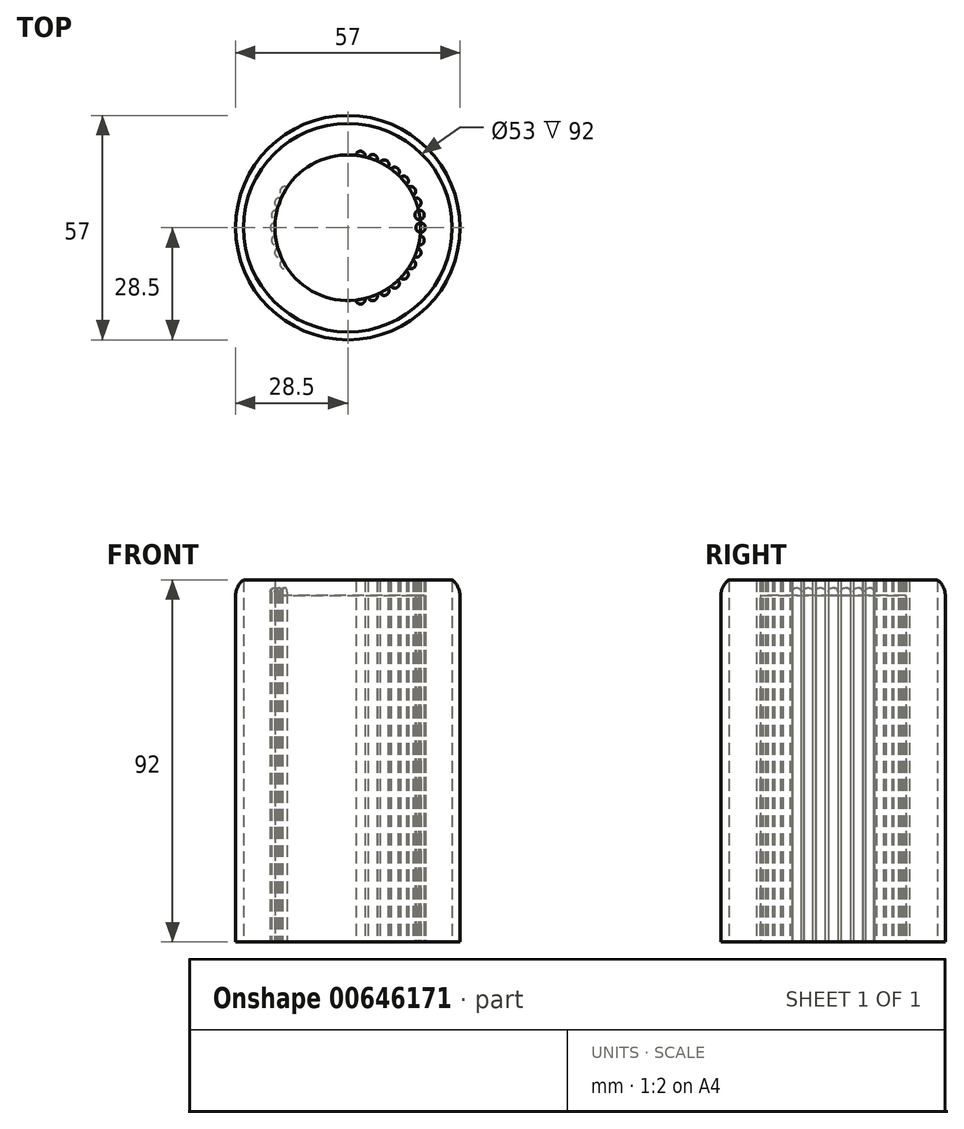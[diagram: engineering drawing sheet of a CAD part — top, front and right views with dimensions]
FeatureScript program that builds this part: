
annotation { "Feature Type Name" : "Feature", "Feature Type Description" : "" }
export const myFeature = defineFeature(function(context is Context, id is Id, definition is map)
    precondition{}
    {
        {
            var Q0;
            Q0=qCreatedBy(makeId("Top.planeOp"),FACE);
            var sketch = newSketch(context, id + "F0", { "sketchPlane" : qUnion([Q0])});
            skCircle(sketch, "E0", {"center": v(0, 0) * mm, "radius": 28.5 * mm});
            skCircle(sketch, "E1", {"center": v(0, 0) * mm, "radius": 26.5 * mm});
            skCircle(sketch, "E2", {"center": v(0, 0) * mm, "radius": 18.5 * mm});
            skLineSegment(sketch, "E3", {"start": v(-44.15, 0) * mm, "end": v(45.98, 0) * mm, "construction": true});
            skPoint(sketch, "E4", {"position": v(-18.5, 0) * mm});
            skCircle(sketch, "E5", {"center": v(-18.5, 0) * mm, "radius": 1.2 * mm});
            skCircle(sketch, "E6.1.0", {"center": v(-18.22, 3.21) * mm, "radius": 1.2 * mm});
            skCircle(sketch, "E6.2.0", {"center": v(-17.38, 6.33) * mm, "radius": 1.2 * mm});
            skLineSegment(sketch, "E6.anchor1", {"start": v(0, 0) * mm, "end": v(-18.5, 0) * mm, "construction": true});
            skLineSegment(sketch, "E6.anchor2", {"start": v(0, 0) * mm, "end": v(-18.22, -3.21) * mm, "construction": true});
            skCircle(sketch, "E7.1.3.0", {"center": v(-16.02, 9.25) * mm, "radius": 1.2 * mm});
            skCircle(sketch, "E7.1.4.0", {"center": v(-14.17, 11.9) * mm, "radius": 1.2 * mm});
            skCircle(sketch, "E7.1.5.0", {"center": v(-11.9, 14.17) * mm, "radius": 1.2 * mm});
            skCircle(sketch, "E7.1.6.0", {"center": v(-9.25, 16.02) * mm, "radius": 1.2 * mm});
            skCircle(sketch, "E7.1.7.0", {"center": v(-6.33, 17.38) * mm, "radius": 1.2 * mm});
            skCircle(sketch, "E7.1.8.0", {"center": v(-3.21, 18.22) * mm, "radius": 1.2 * mm});
            skCircle(sketch, "E7.1.9.0", {"center": v(0, 18.5) * mm, "radius": 1.2 * mm});
            skCircle(sketch, "E7.1.10.0", {"center": v(3.21, 18.22) * mm, "radius": 1.2 * mm});
            skCircle(sketch, "E7.1.11.0", {"center": v(6.33, 17.38) * mm, "radius": 1.2 * mm});
            skCircle(sketch, "E7.1.12.0", {"center": v(9.25, 16.02) * mm, "radius": 1.2 * mm});
            skCircle(sketch, "E7.1.13.0", {"center": v(11.9, 14.17) * mm, "radius": 1.2 * mm});
            skCircle(sketch, "E7.1.14.0", {"center": v(14.17, 11.9) * mm, "radius": 1.2 * mm});
            skCircle(sketch, "E7.1.15.0", {"center": v(16.02, 9.25) * mm, "radius": 1.2 * mm});
            skCircle(sketch, "E7.1.16.0", {"center": v(17.38, 6.33) * mm, "radius": 1.2 * mm});
            skCircle(sketch, "E7.1.17.0", {"center": v(18.22, 3.21) * mm, "radius": 1.2 * mm});
            skCircle(sketch, "E7.1.18.0", {"center": v(18.5, 0) * mm, "radius": 1.2 * mm});
            skCircle(sketch, "E7.1.19.0", {"center": v(18.22, -3.21) * mm, "radius": 1.2 * mm});
            skCircle(sketch, "E7.1.20.0", {"center": v(17.38, -6.33) * mm, "radius": 1.2 * mm});
            skCircle(sketch, "E7.1.21.0", {"center": v(16.02, -9.25) * mm, "radius": 1.2 * mm});
            skCircle(sketch, "E7.1.22.0", {"center": v(14.17, -11.9) * mm, "radius": 1.2 * mm});
            skCircle(sketch, "E7.1.23.0", {"center": v(11.9, -14.17) * mm, "radius": 1.2 * mm});
            skCircle(sketch, "E7.1.24.0", {"center": v(9.25, -16.02) * mm, "radius": 1.2 * mm});
            skCircle(sketch, "E7.1.25.0", {"center": v(6.33, -17.38) * mm, "radius": 1.2 * mm});
            skCircle(sketch, "E7.1.26.0", {"center": v(3.21, -18.22) * mm, "radius": 1.2 * mm});
            skCircle(sketch, "E7.1.27.0", {"center": v(0, -18.5) * mm, "radius": 1.2 * mm});
            skCircle(sketch, "E7.1.28.0", {"center": v(-3.21, -18.22) * mm, "radius": 1.2 * mm});
            skCircle(sketch, "E7.1.29.0", {"center": v(-6.33, -17.38) * mm, "radius": 1.2 * mm});
            skCircle(sketch, "E8.1.30.0", {"center": v(-9.25, -16.02) * mm, "radius": 1.2 * mm});
            skCircle(sketch, "E8.1.31.0", {"center": v(-11.9, -14.17) * mm, "radius": 1.2 * mm});
            skCircle(sketch, "E8.1.32.0", {"center": v(-14.17, -11.9) * mm, "radius": 1.2 * mm});
            skCircle(sketch, "E8.1.33.0", {"center": v(-16.02, -9.25) * mm, "radius": 1.2 * mm});
            skCircle(sketch, "E8.1.34.0", {"center": v(-17.38, -6.33) * mm, "radius": 1.2 * mm});
            skCircle(sketch, "E8.1.35.0", {"center": v(-18.22, -3.21) * mm, "radius": 1.2 * mm});
            skSolve(sketch);
        }
        {
            var Q0;
            Q0=makeQuery(id+"F0.imprint","IMPRINT",FACE,{"disambiguationData":[TD([[makeQuery(id+"F0.imprint","IMPRINT",EDGE,{"derivedFrom":sQuery(id+"F0.wireOp",EDGE,"E0")}),1.0]])]});
            extrude(context, id + "F1", {"entities" : qUnion([Q0]), "depth" : 92 * mm, "offsetDistance" : 25 * mm});
        }
        {
            var Q0;
            Q0=makeQuery(id+"F1.opExtrude","CAP_EDGE",EDGE,{"disambiguationData":[OSD([sQuery(id+"F0.wireOp",EDGE,"E0")])],"isStart":false});
            fillet(context, id + "F2", {"entities" : qUnion([Q0]), "radius" : 5 * mm, "tangentPropagation" : true, "allowEdgeOverflow" : false});
        }
        {
            var Q0;
            Q0=makeQuery(id+"F0.imprint","IMPRINT",FACE,{"disambiguationData":[TD([[makeQuery(id+"F0.imprint","IMPRINT",EDGE,{"derivedFrom":sQuery(id+"F0.wireOp",EDGE,"E1")}),1.0]])]});
            var Q1;
            {var subQ0=sQuery(id+"F0.wireOp",EDGE,"E2");var subQ1=sQuery(id+"F0.wireOp",EDGE,"E6.1.0");var subQ2=makeQuery(id+"F0.imprint","INTERSECT",VERTEX,{"disambiguationData":[OD(0.0)],"derivedFrom":[subQ1,subQ0]});Q1=makeQuery(id+"F0.imprint","IMPRINT",FACE,{"disambiguationData":[TD([[makeQuery(id+"F0.imprint","IMPRINT",EDGE,{"disambiguationData":[TD([[subQ2,-1.0]])],"derivedFrom":subQ1}),1.0]])]});}
            var Q2;
            {var subQ0=sQuery(id+"F0.wireOp",EDGE,"E2");var subQ1=sQuery(id+"F0.wireOp",EDGE,"E6.2.0");var subQ2=makeQuery(id+"F0.imprint","INTERSECT",VERTEX,{"disambiguationData":[OD(0.0)],"derivedFrom":[subQ1,subQ0]});Q2=makeQuery(id+"F0.imprint","IMPRINT",FACE,{"disambiguationData":[TD([[makeQuery(id+"F0.imprint","IMPRINT",EDGE,{"disambiguationData":[TD([[subQ2,-1.0]])],"derivedFrom":subQ1}),1.0]])]});}
            var Q3;
            {var subQ0=sQuery(id+"F0.wireOp",EDGE,"E2");var subQ1=sQuery(id+"F0.wireOp",EDGE,"E7.1.3.0");var subQ2=makeQuery(id+"F0.imprint","INTERSECT",VERTEX,{"disambiguationData":[OD(0.0)],"derivedFrom":[subQ1,subQ0]});Q3=makeQuery(id+"F0.imprint","IMPRINT",FACE,{"disambiguationData":[TD([[makeQuery(id+"F0.imprint","IMPRINT",EDGE,{"disambiguationData":[TD([[subQ2,-1.0]])],"derivedFrom":subQ1}),1.0]])]});}
            var Q4;
            {var subQ0=sQuery(id+"F0.wireOp",EDGE,"E2");var subQ1=sQuery(id+"F0.wireOp",EDGE,"E7.1.4.0");var subQ2=makeQuery(id+"F0.imprint","INTERSECT",VERTEX,{"disambiguationData":[OD(0.0)],"derivedFrom":[subQ1,subQ0]});Q4=makeQuery(id+"F0.imprint","IMPRINT",FACE,{"disambiguationData":[TD([[makeQuery(id+"F0.imprint","IMPRINT",EDGE,{"disambiguationData":[TD([[subQ2,-1.0]])],"derivedFrom":subQ1}),1.0]])]});}
            var Q5;
            {var subQ0=sQuery(id+"F0.wireOp",EDGE,"E2");var subQ1=sQuery(id+"F0.wireOp",EDGE,"E7.1.5.0");var subQ2=makeQuery(id+"F0.imprint","INTERSECT",VERTEX,{"disambiguationData":[OD(0.0)],"derivedFrom":[subQ1,subQ0]});Q5=makeQuery(id+"F0.imprint","IMPRINT",FACE,{"disambiguationData":[TD([[makeQuery(id+"F0.imprint","IMPRINT",EDGE,{"disambiguationData":[TD([[subQ2,-1.0]])],"derivedFrom":subQ1}),1.0]])]});}
            var Q6;
            {var subQ0=sQuery(id+"F0.wireOp",EDGE,"E2");var subQ1=sQuery(id+"F0.wireOp",EDGE,"E7.1.6.0");var subQ2=makeQuery(id+"F0.imprint","INTERSECT",VERTEX,{"disambiguationData":[OD(0.0)],"derivedFrom":[subQ1,subQ0]});Q6=makeQuery(id+"F0.imprint","IMPRINT",FACE,{"disambiguationData":[TD([[makeQuery(id+"F0.imprint","IMPRINT",EDGE,{"disambiguationData":[TD([[subQ2,-1.0]])],"derivedFrom":subQ1}),1.0]])]});}
            var Q7;
            {var subQ0=sQuery(id+"F0.wireOp",EDGE,"E2");var subQ1=sQuery(id+"F0.wireOp",EDGE,"E7.1.7.0");var subQ2=makeQuery(id+"F0.imprint","INTERSECT",VERTEX,{"disambiguationData":[OD(0.0)],"derivedFrom":[subQ1,subQ0]});Q7=makeQuery(id+"F0.imprint","IMPRINT",FACE,{"disambiguationData":[TD([[makeQuery(id+"F0.imprint","IMPRINT",EDGE,{"disambiguationData":[TD([[subQ2,-1.0]])],"derivedFrom":subQ1}),1.0]])]});}
            var Q8;
            {var subQ0=sQuery(id+"F0.wireOp",EDGE,"E2");var subQ1=sQuery(id+"F0.wireOp",EDGE,"E7.1.8.0");var subQ2=makeQuery(id+"F0.imprint","INTERSECT",VERTEX,{"disambiguationData":[OD(0.0)],"derivedFrom":[subQ1,subQ0]});Q8=makeQuery(id+"F0.imprint","IMPRINT",FACE,{"disambiguationData":[TD([[makeQuery(id+"F0.imprint","IMPRINT",EDGE,{"disambiguationData":[TD([[subQ2,-1.0]])],"derivedFrom":subQ1}),1.0]])]});}
            var Q9;
            {var subQ0=sQuery(id+"F0.wireOp",EDGE,"E2");var subQ1=sQuery(id+"F0.wireOp",EDGE,"E7.1.9.0");var subQ2=makeQuery(id+"F0.imprint","INTERSECT",VERTEX,{"disambiguationData":[OD(0.0)],"derivedFrom":[subQ1,subQ0]});Q9=makeQuery(id+"F0.imprint","IMPRINT",FACE,{"disambiguationData":[TD([[makeQuery(id+"F0.imprint","IMPRINT",EDGE,{"disambiguationData":[TD([[subQ2,-1.0]])],"derivedFrom":subQ1}),1.0]])]});}
            var Q10;
            {var subQ0=sQuery(id+"F0.wireOp",EDGE,"E2");var subQ1=sQuery(id+"F0.wireOp",EDGE,"E5");var subQ2=makeQuery(id+"F0.imprint","INTERSECT",VERTEX,{"disambiguationData":[OD(0.0)],"derivedFrom":[subQ1,subQ0]});Q10=makeQuery(id+"F0.imprint","IMPRINT",FACE,{"disambiguationData":[TD([[makeQuery(id+"F0.imprint","IMPRINT",EDGE,{"disambiguationData":[TD([[subQ2,-1.0]])],"derivedFrom":subQ1}),1.0]])]});}
            var Q11;
            {var subQ0=sQuery(id+"F0.wireOp",EDGE,"E2");var subQ1=sQuery(id+"F0.wireOp",EDGE,"E8.1.35.0");var subQ2=makeQuery(id+"F0.imprint","INTERSECT",VERTEX,{"disambiguationData":[OD(0.0)],"derivedFrom":[subQ1,subQ0]});Q11=makeQuery(id+"F0.imprint","IMPRINT",FACE,{"disambiguationData":[TD([[makeQuery(id+"F0.imprint","IMPRINT",EDGE,{"disambiguationData":[TD([[subQ2,-1.0]])],"derivedFrom":subQ1}),1.0]])]});}
            var Q12;
            {var subQ0=sQuery(id+"F0.wireOp",EDGE,"E2");var subQ1=sQuery(id+"F0.wireOp",EDGE,"E8.1.34.0");var subQ2=makeQuery(id+"F0.imprint","INTERSECT",VERTEX,{"disambiguationData":[OD(0.0)],"derivedFrom":[subQ1,subQ0]});Q12=makeQuery(id+"F0.imprint","IMPRINT",FACE,{"disambiguationData":[TD([[makeQuery(id+"F0.imprint","IMPRINT",EDGE,{"disambiguationData":[TD([[subQ2,-1.0]])],"derivedFrom":subQ1}),1.0]])]});}
            var Q13;
            {var subQ0=sQuery(id+"F0.wireOp",EDGE,"E2");var subQ1=sQuery(id+"F0.wireOp",EDGE,"E8.1.33.0");var subQ2=makeQuery(id+"F0.imprint","INTERSECT",VERTEX,{"disambiguationData":[OD(0.0)],"derivedFrom":[subQ1,subQ0]});Q13=makeQuery(id+"F0.imprint","IMPRINT",FACE,{"disambiguationData":[TD([[makeQuery(id+"F0.imprint","IMPRINT",EDGE,{"disambiguationData":[TD([[subQ2,-1.0]])],"derivedFrom":subQ1}),1.0]])]});}
            var Q14;
            {var subQ0=sQuery(id+"F0.wireOp",EDGE,"E2");var subQ1=sQuery(id+"F0.wireOp",EDGE,"E8.1.32.0");var subQ2=makeQuery(id+"F0.imprint","INTERSECT",VERTEX,{"disambiguationData":[OD(0.0)],"derivedFrom":[subQ1,subQ0]});Q14=makeQuery(id+"F0.imprint","IMPRINT",FACE,{"disambiguationData":[TD([[makeQuery(id+"F0.imprint","IMPRINT",EDGE,{"disambiguationData":[TD([[subQ2,-1.0]])],"derivedFrom":subQ1}),1.0]])]});}
            var Q15;
            {var subQ0=sQuery(id+"F0.wireOp",EDGE,"E2");var subQ1=sQuery(id+"F0.wireOp",EDGE,"E8.1.31.0");var subQ2=makeQuery(id+"F0.imprint","INTERSECT",VERTEX,{"disambiguationData":[OD(0.0)],"derivedFrom":[subQ1,subQ0]});Q15=makeQuery(id+"F0.imprint","IMPRINT",FACE,{"disambiguationData":[TD([[makeQuery(id+"F0.imprint","IMPRINT",EDGE,{"disambiguationData":[TD([[subQ2,-1.0]])],"derivedFrom":subQ1}),1.0]])]});}
            var Q16;
            {var subQ0=sQuery(id+"F0.wireOp",EDGE,"E2");var subQ1=sQuery(id+"F0.wireOp",EDGE,"E8.1.30.0");var subQ2=makeQuery(id+"F0.imprint","INTERSECT",VERTEX,{"disambiguationData":[OD(0.0)],"derivedFrom":[subQ1,subQ0]});Q16=makeQuery(id+"F0.imprint","IMPRINT",FACE,{"disambiguationData":[TD([[makeQuery(id+"F0.imprint","IMPRINT",EDGE,{"disambiguationData":[TD([[subQ2,-1.0]])],"derivedFrom":subQ1}),1.0]])]});}
            var Q17;
            {var subQ0=sQuery(id+"F0.wireOp",EDGE,"E2");var subQ1=sQuery(id+"F0.wireOp",EDGE,"E7.1.29.0");var subQ2=makeQuery(id+"F0.imprint","INTERSECT",VERTEX,{"disambiguationData":[OD(0.0)],"derivedFrom":[subQ1,subQ0]});Q17=makeQuery(id+"F0.imprint","IMPRINT",FACE,{"disambiguationData":[TD([[makeQuery(id+"F0.imprint","IMPRINT",EDGE,{"disambiguationData":[TD([[subQ2,-1.0]])],"derivedFrom":subQ1}),1.0]])]});}
            var Q18;
            {var subQ0=sQuery(id+"F0.wireOp",EDGE,"E2");var subQ1=sQuery(id+"F0.wireOp",EDGE,"E7.1.28.0");var subQ2=makeQuery(id+"F0.imprint","INTERSECT",VERTEX,{"disambiguationData":[OD(0.0)],"derivedFrom":[subQ1,subQ0]});Q18=makeQuery(id+"F0.imprint","IMPRINT",FACE,{"disambiguationData":[TD([[makeQuery(id+"F0.imprint","IMPRINT",EDGE,{"disambiguationData":[TD([[subQ2,-1.0]])],"derivedFrom":subQ1}),1.0]])]});}
            var Q19;
            {var subQ0=sQuery(id+"F0.wireOp",EDGE,"E2");var subQ1=sQuery(id+"F0.wireOp",EDGE,"E7.1.27.0");var subQ2=makeQuery(id+"F0.imprint","INTERSECT",VERTEX,{"disambiguationData":[OD(0.0)],"derivedFrom":[subQ1,subQ0]});Q19=makeQuery(id+"F0.imprint","IMPRINT",FACE,{"disambiguationData":[TD([[makeQuery(id+"F0.imprint","IMPRINT",EDGE,{"disambiguationData":[TD([[subQ2,-1.0]])],"derivedFrom":subQ1}),1.0]])]});}
            extrude(context, id + "F3", {"entities" : qUnion([Q0, Q1, Q2, Q3, Q4, Q5, Q6, Q7, Q8, Q9, Q10, Q11, Q12, Q13, Q14, Q15, Q16, Q17, Q18, Q19]), "depth" : 92 * mm, "offsetDistance" : 25 * mm});
        }
        {
            var Q0;
            {var subQ0=sQuery(id+"F0.wireOp",EDGE,"E2");var subQ1=sQuery(id+"F0.wireOp",EDGE,"E5");var subQ2=makeQuery(id+"F0.imprint","INTERSECT",VERTEX,{"disambiguationData":[OD(0.0)],"derivedFrom":[subQ1,subQ0]});Q0=makeQuery(id+"F0.imprint","IMPRINT",FACE,{"disambiguationData":[TD([[makeQuery(id+"F0.imprint","IMPRINT",EDGE,{"disambiguationData":[TD([[subQ2,1.0]])],"derivedFrom":subQ1}),1.0]])]});}
            var Q1;
            {var subQ0=sQuery(id+"F0.wireOp",EDGE,"E2");var subQ1=sQuery(id+"F0.wireOp",EDGE,"E5");var subQ2=makeQuery(id+"F0.imprint","INTERSECT",VERTEX,{"disambiguationData":[OD(0.0)],"derivedFrom":[subQ1,subQ0]});Q1=makeQuery(id+"F0.imprint","IMPRINT",FACE,{"disambiguationData":[TD([[makeQuery(id+"F0.imprint","IMPRINT",EDGE,{"disambiguationData":[TD([[subQ2,-1.0]])],"derivedFrom":subQ1}),1.0]])]});}
            var Q2;
            {var subQ0=sQuery(id+"F0.wireOp",EDGE,"E2");var subQ1=sQuery(id+"F0.wireOp",EDGE,"E6.1.0");var subQ2=makeQuery(id+"F0.imprint","INTERSECT",VERTEX,{"disambiguationData":[OD(0.0)],"derivedFrom":[subQ1,subQ0]});Q2=makeQuery(id+"F0.imprint","IMPRINT",FACE,{"disambiguationData":[TD([[makeQuery(id+"F0.imprint","IMPRINT",EDGE,{"disambiguationData":[TD([[subQ2,-1.0]])],"derivedFrom":subQ1}),1.0]])]});}
            var Q3;
            {var subQ0=sQuery(id+"F0.wireOp",EDGE,"E2");var subQ1=sQuery(id+"F0.wireOp",EDGE,"E6.1.0");var subQ2=makeQuery(id+"F0.imprint","INTERSECT",VERTEX,{"disambiguationData":[OD(0.0)],"derivedFrom":[subQ1,subQ0]});Q3=makeQuery(id+"F0.imprint","IMPRINT",FACE,{"disambiguationData":[TD([[makeQuery(id+"F0.imprint","IMPRINT",EDGE,{"disambiguationData":[TD([[subQ2,1.0]])],"derivedFrom":subQ1}),1.0]])]});}
            var Q4;
            {var subQ0=sQuery(id+"F0.wireOp",EDGE,"E2");var subQ1=sQuery(id+"F0.wireOp",EDGE,"E6.2.0");var subQ2=makeQuery(id+"F0.imprint","INTERSECT",VERTEX,{"disambiguationData":[OD(0.0)],"derivedFrom":[subQ1,subQ0]});Q4=makeQuery(id+"F0.imprint","IMPRINT",FACE,{"disambiguationData":[TD([[makeQuery(id+"F0.imprint","IMPRINT",EDGE,{"disambiguationData":[TD([[subQ2,1.0]])],"derivedFrom":subQ1}),1.0]])]});}
            var Q5;
            {var subQ0=sQuery(id+"F0.wireOp",EDGE,"E2");var subQ1=sQuery(id+"F0.wireOp",EDGE,"E6.2.0");var subQ2=makeQuery(id+"F0.imprint","INTERSECT",VERTEX,{"disambiguationData":[OD(0.0)],"derivedFrom":[subQ1,subQ0]});Q5=makeQuery(id+"F0.imprint","IMPRINT",FACE,{"disambiguationData":[TD([[makeQuery(id+"F0.imprint","IMPRINT",EDGE,{"disambiguationData":[TD([[subQ2,-1.0]])],"derivedFrom":subQ1}),1.0]])]});}
            var Q6;
            {var subQ0=sQuery(id+"F0.wireOp",EDGE,"E2");var subQ1=sQuery(id+"F0.wireOp",EDGE,"E7.1.3.0");var subQ2=makeQuery(id+"F0.imprint","INTERSECT",VERTEX,{"disambiguationData":[OD(0.0)],"derivedFrom":[subQ1,subQ0]});Q6=makeQuery(id+"F0.imprint","IMPRINT",FACE,{"disambiguationData":[TD([[makeQuery(id+"F0.imprint","IMPRINT",EDGE,{"disambiguationData":[TD([[subQ2,-1.0]])],"derivedFrom":subQ1}),1.0]])]});}
            var Q7;
            {var subQ0=sQuery(id+"F0.wireOp",EDGE,"E2");var subQ1=sQuery(id+"F0.wireOp",EDGE,"E7.1.3.0");var subQ2=makeQuery(id+"F0.imprint","INTERSECT",VERTEX,{"disambiguationData":[OD(0.0)],"derivedFrom":[subQ1,subQ0]});Q7=makeQuery(id+"F0.imprint","IMPRINT",FACE,{"disambiguationData":[TD([[makeQuery(id+"F0.imprint","IMPRINT",EDGE,{"disambiguationData":[TD([[subQ2,1.0]])],"derivedFrom":subQ1}),1.0]])]});}
            var Q8;
            {var subQ0=sQuery(id+"F0.wireOp",EDGE,"E2");var subQ1=sQuery(id+"F0.wireOp",EDGE,"E8.1.35.0");var subQ2=makeQuery(id+"F0.imprint","INTERSECT",VERTEX,{"disambiguationData":[OD(0.0)],"derivedFrom":[subQ1,subQ0]});Q8=makeQuery(id+"F0.imprint","IMPRINT",FACE,{"disambiguationData":[TD([[makeQuery(id+"F0.imprint","IMPRINT",EDGE,{"disambiguationData":[TD([[subQ2,-1.0]])],"derivedFrom":subQ1}),1.0]])]});}
            var Q9;
            {var subQ0=sQuery(id+"F0.wireOp",EDGE,"E2");var subQ1=sQuery(id+"F0.wireOp",EDGE,"E8.1.35.0");var subQ2=makeQuery(id+"F0.imprint","INTERSECT",VERTEX,{"disambiguationData":[OD(0.0)],"derivedFrom":[subQ1,subQ0]});Q9=makeQuery(id+"F0.imprint","IMPRINT",FACE,{"disambiguationData":[TD([[makeQuery(id+"F0.imprint","IMPRINT",EDGE,{"disambiguationData":[TD([[subQ2,1.0]])],"derivedFrom":subQ1}),1.0]])]});}
            var Q10;
            {var subQ0=sQuery(id+"F0.wireOp",EDGE,"E2");var subQ1=sQuery(id+"F0.wireOp",EDGE,"E8.1.34.0");var subQ2=makeQuery(id+"F0.imprint","INTERSECT",VERTEX,{"disambiguationData":[OD(0.0)],"derivedFrom":[subQ1,subQ0]});Q10=makeQuery(id+"F0.imprint","IMPRINT",FACE,{"disambiguationData":[TD([[makeQuery(id+"F0.imprint","IMPRINT",EDGE,{"disambiguationData":[TD([[subQ2,-1.0]])],"derivedFrom":subQ1}),1.0]])]});}
            var Q11;
            {var subQ0=sQuery(id+"F0.wireOp",EDGE,"E2");var subQ1=sQuery(id+"F0.wireOp",EDGE,"E8.1.34.0");var subQ2=makeQuery(id+"F0.imprint","INTERSECT",VERTEX,{"disambiguationData":[OD(0.0)],"derivedFrom":[subQ1,subQ0]});Q11=makeQuery(id+"F0.imprint","IMPRINT",FACE,{"disambiguationData":[TD([[makeQuery(id+"F0.imprint","IMPRINT",EDGE,{"disambiguationData":[TD([[subQ2,1.0]])],"derivedFrom":subQ1}),1.0]])]});}
            var Q12;
            {var subQ0=sQuery(id+"F0.wireOp",EDGE,"E2");var subQ1=sQuery(id+"F0.wireOp",EDGE,"E8.1.33.0");var subQ2=makeQuery(id+"F0.imprint","INTERSECT",VERTEX,{"disambiguationData":[OD(0.0)],"derivedFrom":[subQ1,subQ0]});Q12=makeQuery(id+"F0.imprint","IMPRINT",FACE,{"disambiguationData":[TD([[makeQuery(id+"F0.imprint","IMPRINT",EDGE,{"disambiguationData":[TD([[subQ2,-1.0]])],"derivedFrom":subQ1}),1.0]])]});}
            var Q13;
            {var subQ0=sQuery(id+"F0.wireOp",EDGE,"E2");var subQ1=sQuery(id+"F0.wireOp",EDGE,"E8.1.33.0");var subQ2=makeQuery(id+"F0.imprint","INTERSECT",VERTEX,{"disambiguationData":[OD(0.0)],"derivedFrom":[subQ1,subQ0]});Q13=makeQuery(id+"F0.imprint","IMPRINT",FACE,{"disambiguationData":[TD([[makeQuery(id+"F0.imprint","IMPRINT",EDGE,{"disambiguationData":[TD([[subQ2,1.0]])],"derivedFrom":subQ1}),1.0]])]});}
            extrude(context, id + "F4", {"entities" : qUnion([Q0, Q1, Q2, Q3, Q4, Q5, Q6, Q7, Q8, Q9, Q10, Q11, Q12, Q13]), "operationType" : NewBodyOperationType.REMOVE, "oppositeDirection" : true, "depth" : -90 * mm, "offsetDistance" : 25 * mm});
        }
        {
            var Q0;
            Q0=makeQuery(id+"F4.boolean.opBoolean","COPY",EDGE,{"derivedFrom":makeQuery(id+"F4.opExtrude","CAP_EDGE",EDGE,{"disambiguationData":[OSD([sQuery(id+"F0.wireOp",EDGE,"E8.1.33.0")])],"isStart":false})});
            var Q1;
            Q1=makeQuery(id+"F4.boolean.opBoolean","COPY",EDGE,{"derivedFrom":makeQuery(id+"F4.opExtrude","CAP_EDGE",EDGE,{"disambiguationData":[OSD([sQuery(id+"F0.wireOp",EDGE,"E8.1.34.0")])],"isStart":false})});
            var Q2;
            Q2=makeQuery(id+"F4.boolean.opBoolean","COPY",EDGE,{"derivedFrom":makeQuery(id+"F4.opExtrude","CAP_EDGE",EDGE,{"disambiguationData":[OSD([sQuery(id+"F0.wireOp",EDGE,"E8.1.35.0")])],"isStart":false})});
            var Q3;
            Q3=makeQuery(id+"F4.boolean.opBoolean","COPY",EDGE,{"derivedFrom":makeQuery(id+"F4.opExtrude","CAP_EDGE",EDGE,{"disambiguationData":[OSD([sQuery(id+"F0.wireOp",EDGE,"E5")])],"isStart":false})});
            var Q4;
            Q4=makeQuery(id+"F4.boolean.opBoolean","COPY",EDGE,{"derivedFrom":makeQuery(id+"F4.opExtrude","CAP_EDGE",EDGE,{"disambiguationData":[OSD([sQuery(id+"F0.wireOp",EDGE,"E6.1.0")])],"isStart":false})});
            var Q5;
            Q5=makeQuery(id+"F4.boolean.opBoolean","COPY",EDGE,{"derivedFrom":makeQuery(id+"F4.opExtrude","CAP_EDGE",EDGE,{"disambiguationData":[OSD([sQuery(id+"F0.wireOp",EDGE,"E6.2.0")])],"isStart":false})});
            var Q6;
            Q6=makeQuery(id+"F4.boolean.opBoolean","COPY",EDGE,{"derivedFrom":makeQuery(id+"F4.opExtrude","CAP_EDGE",EDGE,{"disambiguationData":[OSD([sQuery(id+"F0.wireOp",EDGE,"E7.1.3.0")])],"isStart":false})});
            fillet(context, id + "F5", {"entities" : qUnion([Q0, Q1, Q2, Q3, Q4, Q5, Q6]), "radius" : 1 * mm, "tangentPropagation" : true, "allowEdgeOverflow" : false});
        }
        {
            var Q0;
            {var subQ0=sQuery(id+"F0.wireOp",EDGE,"E2");var subQ53=sQuery(id+"F0.wireOp",EDGE,"E5");var subQ58=makeQuery(id+"F0.imprint","INTERSECT",VERTEX,{"disambiguationData":[OD(0.0)],"derivedFrom":[subQ53,subQ0]});Q0=makeQuery(id+"F0.imprint","IMPRINT",FACE,{"disambiguationData":[TD([[makeQuery(id+"F0.imprint","IMPRINT",EDGE,{"disambiguationData":[TD([[subQ58,1.0]])],"derivedFrom":subQ53}),-1.0]])]});}
            var Q1;
            {var subQ0=sQuery(id+"F0.wireOp",EDGE,"E2");var subQ1=sQuery(id+"F0.wireOp",EDGE,"E7.1.14.0");var subQ2=makeQuery(id+"F0.imprint","INTERSECT",VERTEX,{"disambiguationData":[OD(0.0)],"derivedFrom":[subQ1,subQ0]});Q1=makeQuery(id+"F0.imprint","IMPRINT",FACE,{"disambiguationData":[TD([[makeQuery(id+"F0.imprint","IMPRINT",EDGE,{"disambiguationData":[TD([[subQ2,1.0]])],"derivedFrom":subQ1}),1.0]])]});}
            var Q2;
            {var subQ0=sQuery(id+"F0.wireOp",EDGE,"E2");var subQ1=sQuery(id+"F0.wireOp",EDGE,"E7.1.15.0");var subQ2=makeQuery(id+"F0.imprint","INTERSECT",VERTEX,{"disambiguationData":[OD(0.0)],"derivedFrom":[subQ1,subQ0]});Q2=makeQuery(id+"F0.imprint","IMPRINT",FACE,{"disambiguationData":[TD([[makeQuery(id+"F0.imprint","IMPRINT",EDGE,{"disambiguationData":[TD([[subQ2,1.0]])],"derivedFrom":subQ1}),1.0]])]});}
            var Q3;
            {var subQ0=sQuery(id+"F0.wireOp",EDGE,"E2");var subQ1=sQuery(id+"F0.wireOp",EDGE,"E7.1.16.0");var subQ2=makeQuery(id+"F0.imprint","INTERSECT",VERTEX,{"disambiguationData":[OD(0.0)],"derivedFrom":[subQ1,subQ0]});Q3=makeQuery(id+"F0.imprint","IMPRINT",FACE,{"disambiguationData":[TD([[makeQuery(id+"F0.imprint","IMPRINT",EDGE,{"disambiguationData":[TD([[subQ2,1.0]])],"derivedFrom":subQ1}),1.0]])]});}
            var Q4;
            {var subQ0=sQuery(id+"F0.wireOp",EDGE,"E2");var subQ1=sQuery(id+"F0.wireOp",EDGE,"E7.1.17.0");var subQ2=makeQuery(id+"F0.imprint","INTERSECT",VERTEX,{"disambiguationData":[OD(0.0)],"derivedFrom":[subQ1,subQ0]});Q4=makeQuery(id+"F0.imprint","IMPRINT",FACE,{"disambiguationData":[TD([[makeQuery(id+"F0.imprint","IMPRINT",EDGE,{"disambiguationData":[TD([[subQ2,-1.0]])],"derivedFrom":subQ1}),1.0]])]});}
            var Q5;
            {var subQ0=sQuery(id+"F0.wireOp",EDGE,"E2");var subQ1=sQuery(id+"F0.wireOp",EDGE,"E7.1.18.0");var subQ2=makeQuery(id+"F0.imprint","INTERSECT",VERTEX,{"disambiguationData":[OD(0.0)],"derivedFrom":[subQ1,subQ0]});Q5=makeQuery(id+"F0.imprint","IMPRINT",FACE,{"disambiguationData":[TD([[makeQuery(id+"F0.imprint","IMPRINT",EDGE,{"disambiguationData":[TD([[subQ2,1.0]])],"derivedFrom":subQ1}),1.0]])]});}
            var Q6;
            {var subQ0=sQuery(id+"F0.wireOp",EDGE,"E2");var subQ1=sQuery(id+"F0.wireOp",EDGE,"E7.1.19.0");var subQ2=makeQuery(id+"F0.imprint","INTERSECT",VERTEX,{"disambiguationData":[OD(0.0)],"derivedFrom":[subQ1,subQ0]});Q6=makeQuery(id+"F0.imprint","IMPRINT",FACE,{"disambiguationData":[TD([[makeQuery(id+"F0.imprint","IMPRINT",EDGE,{"disambiguationData":[TD([[subQ2,1.0]])],"derivedFrom":subQ1}),1.0]])]});}
            var Q7;
            {var subQ0=sQuery(id+"F0.wireOp",EDGE,"E2");var subQ1=sQuery(id+"F0.wireOp",EDGE,"E7.1.20.0");var subQ2=makeQuery(id+"F0.imprint","INTERSECT",VERTEX,{"disambiguationData":[OD(0.0)],"derivedFrom":[subQ1,subQ0]});Q7=makeQuery(id+"F0.imprint","IMPRINT",FACE,{"disambiguationData":[TD([[makeQuery(id+"F0.imprint","IMPRINT",EDGE,{"disambiguationData":[TD([[subQ2,1.0]])],"derivedFrom":subQ1}),1.0]])]});}
            var Q8;
            {var subQ0=sQuery(id+"F0.wireOp",EDGE,"E2");var subQ1=sQuery(id+"F0.wireOp",EDGE,"E7.1.21.0");var subQ2=makeQuery(id+"F0.imprint","INTERSECT",VERTEX,{"disambiguationData":[OD(0.0)],"derivedFrom":[subQ1,subQ0]});Q8=makeQuery(id+"F0.imprint","IMPRINT",FACE,{"disambiguationData":[TD([[makeQuery(id+"F0.imprint","IMPRINT",EDGE,{"disambiguationData":[TD([[subQ2,1.0]])],"derivedFrom":subQ1}),1.0]])]});}
            var Q9;
            {var subQ0=sQuery(id+"F0.wireOp",EDGE,"E2");var subQ1=sQuery(id+"F0.wireOp",EDGE,"E7.1.13.0");var subQ2=makeQuery(id+"F0.imprint","INTERSECT",VERTEX,{"disambiguationData":[OD(0.0)],"derivedFrom":[subQ1,subQ0]});Q9=makeQuery(id+"F0.imprint","IMPRINT",FACE,{"disambiguationData":[TD([[makeQuery(id+"F0.imprint","IMPRINT",EDGE,{"disambiguationData":[TD([[subQ2,1.0]])],"derivedFrom":subQ1}),1.0]])]});}
            var Q10;
            {var subQ0=sQuery(id+"F0.wireOp",EDGE,"E2");var subQ1=sQuery(id+"F0.wireOp",EDGE,"E6.1.0");var subQ2=makeQuery(id+"F0.imprint","INTERSECT",VERTEX,{"disambiguationData":[OD(0.0)],"derivedFrom":[subQ1,subQ0]});Q10=makeQuery(id+"F0.imprint","IMPRINT",FACE,{"disambiguationData":[TD([[makeQuery(id+"F0.imprint","IMPRINT",EDGE,{"disambiguationData":[TD([[subQ2,1.0]])],"derivedFrom":subQ1}),1.0]])]});}
            var Q11;
            {var subQ0=sQuery(id+"F0.wireOp",EDGE,"E2");var subQ1=sQuery(id+"F0.wireOp",EDGE,"E6.2.0");var subQ2=makeQuery(id+"F0.imprint","INTERSECT",VERTEX,{"disambiguationData":[OD(0.0)],"derivedFrom":[subQ1,subQ0]});Q11=makeQuery(id+"F0.imprint","IMPRINT",FACE,{"disambiguationData":[TD([[makeQuery(id+"F0.imprint","IMPRINT",EDGE,{"disambiguationData":[TD([[subQ2,1.0]])],"derivedFrom":subQ1}),1.0]])]});}
            var Q12;
            {var subQ0=sQuery(id+"F0.wireOp",EDGE,"E2");var subQ1=sQuery(id+"F0.wireOp",EDGE,"E7.1.3.0");var subQ2=makeQuery(id+"F0.imprint","INTERSECT",VERTEX,{"disambiguationData":[OD(0.0)],"derivedFrom":[subQ1,subQ0]});Q12=makeQuery(id+"F0.imprint","IMPRINT",FACE,{"disambiguationData":[TD([[makeQuery(id+"F0.imprint","IMPRINT",EDGE,{"disambiguationData":[TD([[subQ2,1.0]])],"derivedFrom":subQ1}),1.0]])]});}
            var Q13;
            {var subQ0=sQuery(id+"F0.wireOp",EDGE,"E2");var subQ1=sQuery(id+"F0.wireOp",EDGE,"E7.1.4.0");var subQ2=makeQuery(id+"F0.imprint","INTERSECT",VERTEX,{"disambiguationData":[OD(0.0)],"derivedFrom":[subQ1,subQ0]});Q13=makeQuery(id+"F0.imprint","IMPRINT",FACE,{"disambiguationData":[TD([[makeQuery(id+"F0.imprint","IMPRINT",EDGE,{"disambiguationData":[TD([[subQ2,1.0]])],"derivedFrom":subQ1}),1.0]])]});}
            var Q14;
            {var subQ0=sQuery(id+"F0.wireOp",EDGE,"E2");var subQ1=sQuery(id+"F0.wireOp",EDGE,"E7.1.5.0");var subQ2=makeQuery(id+"F0.imprint","INTERSECT",VERTEX,{"disambiguationData":[OD(0.0)],"derivedFrom":[subQ1,subQ0]});Q14=makeQuery(id+"F0.imprint","IMPRINT",FACE,{"disambiguationData":[TD([[makeQuery(id+"F0.imprint","IMPRINT",EDGE,{"disambiguationData":[TD([[subQ2,1.0]])],"derivedFrom":subQ1}),1.0]])]});}
            var Q15;
            {var subQ0=sQuery(id+"F0.wireOp",EDGE,"E2");var subQ1=sQuery(id+"F0.wireOp",EDGE,"E7.1.6.0");var subQ2=makeQuery(id+"F0.imprint","INTERSECT",VERTEX,{"disambiguationData":[OD(0.0)],"derivedFrom":[subQ1,subQ0]});Q15=makeQuery(id+"F0.imprint","IMPRINT",FACE,{"disambiguationData":[TD([[makeQuery(id+"F0.imprint","IMPRINT",EDGE,{"disambiguationData":[TD([[subQ2,1.0]])],"derivedFrom":subQ1}),1.0]])]});}
            var Q16;
            {var subQ0=sQuery(id+"F0.wireOp",EDGE,"E2");var subQ1=sQuery(id+"F0.wireOp",EDGE,"E7.1.7.0");var subQ2=makeQuery(id+"F0.imprint","INTERSECT",VERTEX,{"disambiguationData":[OD(0.0)],"derivedFrom":[subQ1,subQ0]});Q16=makeQuery(id+"F0.imprint","IMPRINT",FACE,{"disambiguationData":[TD([[makeQuery(id+"F0.imprint","IMPRINT",EDGE,{"disambiguationData":[TD([[subQ2,1.0]])],"derivedFrom":subQ1}),1.0]])]});}
            var Q17;
            {var subQ0=sQuery(id+"F0.wireOp",EDGE,"E2");var subQ1=sQuery(id+"F0.wireOp",EDGE,"E5");var subQ2=makeQuery(id+"F0.imprint","INTERSECT",VERTEX,{"disambiguationData":[OD(0.0)],"derivedFrom":[subQ1,subQ0]});Q17=makeQuery(id+"F0.imprint","IMPRINT",FACE,{"disambiguationData":[TD([[makeQuery(id+"F0.imprint","IMPRINT",EDGE,{"disambiguationData":[TD([[subQ2,1.0]])],"derivedFrom":subQ1}),1.0]])]});}
            var Q18;
            {var subQ0=sQuery(id+"F0.wireOp",EDGE,"E2");var subQ1=sQuery(id+"F0.wireOp",EDGE,"E8.1.35.0");var subQ2=makeQuery(id+"F0.imprint","INTERSECT",VERTEX,{"disambiguationData":[OD(0.0)],"derivedFrom":[subQ1,subQ0]});Q18=makeQuery(id+"F0.imprint","IMPRINT",FACE,{"disambiguationData":[TD([[makeQuery(id+"F0.imprint","IMPRINT",EDGE,{"disambiguationData":[TD([[subQ2,1.0]])],"derivedFrom":subQ1}),1.0]])]});}
            var Q19;
            {var subQ0=sQuery(id+"F0.wireOp",EDGE,"E2");var subQ1=sQuery(id+"F0.wireOp",EDGE,"E8.1.34.0");var subQ2=makeQuery(id+"F0.imprint","INTERSECT",VERTEX,{"disambiguationData":[OD(0.0)],"derivedFrom":[subQ1,subQ0]});Q19=makeQuery(id+"F0.imprint","IMPRINT",FACE,{"disambiguationData":[TD([[makeQuery(id+"F0.imprint","IMPRINT",EDGE,{"disambiguationData":[TD([[subQ2,1.0]])],"derivedFrom":subQ1}),1.0]])]});}
            var Q20;
            {var subQ0=sQuery(id+"F0.wireOp",EDGE,"E2");var subQ1=sQuery(id+"F0.wireOp",EDGE,"E8.1.33.0");var subQ2=makeQuery(id+"F0.imprint","INTERSECT",VERTEX,{"disambiguationData":[OD(0.0)],"derivedFrom":[subQ1,subQ0]});Q20=makeQuery(id+"F0.imprint","IMPRINT",FACE,{"disambiguationData":[TD([[makeQuery(id+"F0.imprint","IMPRINT",EDGE,{"disambiguationData":[TD([[subQ2,1.0]])],"derivedFrom":subQ1}),1.0]])]});}
            var Q21;
            {var subQ0=sQuery(id+"F0.wireOp",EDGE,"E2");var subQ1=sQuery(id+"F0.wireOp",EDGE,"E8.1.32.0");var subQ2=makeQuery(id+"F0.imprint","INTERSECT",VERTEX,{"disambiguationData":[OD(0.0)],"derivedFrom":[subQ1,subQ0]});Q21=makeQuery(id+"F0.imprint","IMPRINT",FACE,{"disambiguationData":[TD([[makeQuery(id+"F0.imprint","IMPRINT",EDGE,{"disambiguationData":[TD([[subQ2,1.0]])],"derivedFrom":subQ1}),1.0]])]});}
            var Q22;
            {var subQ0=sQuery(id+"F0.wireOp",EDGE,"E2");var subQ1=sQuery(id+"F0.wireOp",EDGE,"E8.1.31.0");var subQ2=makeQuery(id+"F0.imprint","INTERSECT",VERTEX,{"disambiguationData":[OD(0.0)],"derivedFrom":[subQ1,subQ0]});Q22=makeQuery(id+"F0.imprint","IMPRINT",FACE,{"disambiguationData":[TD([[makeQuery(id+"F0.imprint","IMPRINT",EDGE,{"disambiguationData":[TD([[subQ2,1.0]])],"derivedFrom":subQ1}),1.0]])]});}
            var Q23;
            {var subQ0=sQuery(id+"F0.wireOp",EDGE,"E2");var subQ1=sQuery(id+"F0.wireOp",EDGE,"E8.1.30.0");var subQ2=makeQuery(id+"F0.imprint","INTERSECT",VERTEX,{"disambiguationData":[OD(0.0)],"derivedFrom":[subQ1,subQ0]});Q23=makeQuery(id+"F0.imprint","IMPRINT",FACE,{"disambiguationData":[TD([[makeQuery(id+"F0.imprint","IMPRINT",EDGE,{"disambiguationData":[TD([[subQ2,1.0]])],"derivedFrom":subQ1}),1.0]])]});}
            var Q24;
            {var subQ0=sQuery(id+"F0.wireOp",EDGE,"E2");var subQ1=sQuery(id+"F0.wireOp",EDGE,"E7.1.29.0");var subQ2=makeQuery(id+"F0.imprint","INTERSECT",VERTEX,{"disambiguationData":[OD(0.0)],"derivedFrom":[subQ1,subQ0]});Q24=makeQuery(id+"F0.imprint","IMPRINT",FACE,{"disambiguationData":[TD([[makeQuery(id+"F0.imprint","IMPRINT",EDGE,{"disambiguationData":[TD([[subQ2,1.0]])],"derivedFrom":subQ1}),1.0]])]});}
            var Q25;
            {var subQ0=sQuery(id+"F0.wireOp",EDGE,"E2");var subQ1=sQuery(id+"F0.wireOp",EDGE,"E7.1.8.0");var subQ2=makeQuery(id+"F0.imprint","INTERSECT",VERTEX,{"disambiguationData":[OD(0.0)],"derivedFrom":[subQ1,subQ0]});Q25=makeQuery(id+"F0.imprint","IMPRINT",FACE,{"disambiguationData":[TD([[makeQuery(id+"F0.imprint","IMPRINT",EDGE,{"disambiguationData":[TD([[subQ2,1.0]])],"derivedFrom":subQ1}),1.0]])]});}
            var Q26;
            {var subQ0=sQuery(id+"F0.wireOp",EDGE,"E2");var subQ1=sQuery(id+"F0.wireOp",EDGE,"E7.1.9.0");var subQ2=makeQuery(id+"F0.imprint","INTERSECT",VERTEX,{"disambiguationData":[OD(0.0)],"derivedFrom":[subQ1,subQ0]});Q26=makeQuery(id+"F0.imprint","IMPRINT",FACE,{"disambiguationData":[TD([[makeQuery(id+"F0.imprint","IMPRINT",EDGE,{"disambiguationData":[TD([[subQ2,1.0]])],"derivedFrom":subQ1}),1.0]])]});}
            var Q27;
            {var subQ0=sQuery(id+"F0.wireOp",EDGE,"E2");var subQ1=sQuery(id+"F0.wireOp",EDGE,"E7.1.10.0");var subQ2=makeQuery(id+"F0.imprint","INTERSECT",VERTEX,{"disambiguationData":[OD(0.0)],"derivedFrom":[subQ1,subQ0]});Q27=makeQuery(id+"F0.imprint","IMPRINT",FACE,{"disambiguationData":[TD([[makeQuery(id+"F0.imprint","IMPRINT",EDGE,{"disambiguationData":[TD([[subQ2,1.0]])],"derivedFrom":subQ1}),1.0]])]});}
            var Q28;
            {var subQ0=sQuery(id+"F0.wireOp",EDGE,"E2");var subQ1=sQuery(id+"F0.wireOp",EDGE,"E7.1.11.0");var subQ2=makeQuery(id+"F0.imprint","INTERSECT",VERTEX,{"disambiguationData":[OD(0.0)],"derivedFrom":[subQ1,subQ0]});Q28=makeQuery(id+"F0.imprint","IMPRINT",FACE,{"disambiguationData":[TD([[makeQuery(id+"F0.imprint","IMPRINT",EDGE,{"disambiguationData":[TD([[subQ2,1.0]])],"derivedFrom":subQ1}),1.0]])]});}
            var Q29;
            {var subQ0=sQuery(id+"F0.wireOp",EDGE,"E2");var subQ1=sQuery(id+"F0.wireOp",EDGE,"E7.1.12.0");var subQ2=makeQuery(id+"F0.imprint","INTERSECT",VERTEX,{"disambiguationData":[OD(0.0)],"derivedFrom":[subQ1,subQ0]});Q29=makeQuery(id+"F0.imprint","IMPRINT",FACE,{"disambiguationData":[TD([[makeQuery(id+"F0.imprint","IMPRINT",EDGE,{"disambiguationData":[TD([[subQ2,1.0]])],"derivedFrom":subQ1}),1.0]])]});}
            var Q30;
            {var subQ0=sQuery(id+"F0.wireOp",EDGE,"E2");var subQ1=sQuery(id+"F0.wireOp",EDGE,"E7.1.22.0");var subQ2=makeQuery(id+"F0.imprint","INTERSECT",VERTEX,{"disambiguationData":[OD(0.0)],"derivedFrom":[subQ1,subQ0]});Q30=makeQuery(id+"F0.imprint","IMPRINT",FACE,{"disambiguationData":[TD([[makeQuery(id+"F0.imprint","IMPRINT",EDGE,{"disambiguationData":[TD([[subQ2,1.0]])],"derivedFrom":subQ1}),1.0]])]});}
            var Q31;
            {var subQ0=sQuery(id+"F0.wireOp",EDGE,"E2");var subQ1=sQuery(id+"F0.wireOp",EDGE,"E7.1.23.0");var subQ2=makeQuery(id+"F0.imprint","INTERSECT",VERTEX,{"disambiguationData":[OD(0.0)],"derivedFrom":[subQ1,subQ0]});Q31=makeQuery(id+"F0.imprint","IMPRINT",FACE,{"disambiguationData":[TD([[makeQuery(id+"F0.imprint","IMPRINT",EDGE,{"disambiguationData":[TD([[subQ2,1.0]])],"derivedFrom":subQ1}),1.0]])]});}
            var Q32;
            {var subQ0=sQuery(id+"F0.wireOp",EDGE,"E2");var subQ1=sQuery(id+"F0.wireOp",EDGE,"E7.1.24.0");var subQ2=makeQuery(id+"F0.imprint","INTERSECT",VERTEX,{"disambiguationData":[OD(0.0)],"derivedFrom":[subQ1,subQ0]});Q32=makeQuery(id+"F0.imprint","IMPRINT",FACE,{"disambiguationData":[TD([[makeQuery(id+"F0.imprint","IMPRINT",EDGE,{"disambiguationData":[TD([[subQ2,1.0]])],"derivedFrom":subQ1}),1.0]])]});}
            var Q33;
            {var subQ0=sQuery(id+"F0.wireOp",EDGE,"E2");var subQ1=sQuery(id+"F0.wireOp",EDGE,"E7.1.25.0");var subQ2=makeQuery(id+"F0.imprint","INTERSECT",VERTEX,{"disambiguationData":[OD(0.0)],"derivedFrom":[subQ1,subQ0]});Q33=makeQuery(id+"F0.imprint","IMPRINT",FACE,{"disambiguationData":[TD([[makeQuery(id+"F0.imprint","IMPRINT",EDGE,{"disambiguationData":[TD([[subQ2,1.0]])],"derivedFrom":subQ1}),1.0]])]});}
            var Q34;
            {var subQ0=sQuery(id+"F0.wireOp",EDGE,"E2");var subQ1=sQuery(id+"F0.wireOp",EDGE,"E7.1.26.0");var subQ2=makeQuery(id+"F0.imprint","INTERSECT",VERTEX,{"disambiguationData":[OD(0.0)],"derivedFrom":[subQ1,subQ0]});Q34=makeQuery(id+"F0.imprint","IMPRINT",FACE,{"disambiguationData":[TD([[makeQuery(id+"F0.imprint","IMPRINT",EDGE,{"disambiguationData":[TD([[subQ2,1.0]])],"derivedFrom":subQ1}),1.0]])]});}
            var Q35;
            {var subQ0=sQuery(id+"F0.wireOp",EDGE,"E2");var subQ1=sQuery(id+"F0.wireOp",EDGE,"E7.1.27.0");var subQ2=makeQuery(id+"F0.imprint","INTERSECT",VERTEX,{"disambiguationData":[OD(0.0)],"derivedFrom":[subQ1,subQ0]});Q35=makeQuery(id+"F0.imprint","IMPRINT",FACE,{"disambiguationData":[TD([[makeQuery(id+"F0.imprint","IMPRINT",EDGE,{"disambiguationData":[TD([[subQ2,1.0]])],"derivedFrom":subQ1}),1.0]])]});}
            var Q36;
            {var subQ0=sQuery(id+"F0.wireOp",EDGE,"E2");var subQ1=sQuery(id+"F0.wireOp",EDGE,"E7.1.28.0");var subQ2=makeQuery(id+"F0.imprint","INTERSECT",VERTEX,{"disambiguationData":[OD(0.0)],"derivedFrom":[subQ1,subQ0]});Q36=makeQuery(id+"F0.imprint","IMPRINT",FACE,{"disambiguationData":[TD([[makeQuery(id+"F0.imprint","IMPRINT",EDGE,{"disambiguationData":[TD([[subQ2,1.0]])],"derivedFrom":subQ1}),1.0]])]});}
            extrude(context, id + "F6", {"entities" : qUnion([Q0, Q1, Q2, Q3, Q4, Q5, Q6, Q7, Q8, Q9, Q10, Q11, Q12, Q13, Q14, Q15, Q16, Q17, Q18, Q19, Q20, Q21, Q22, Q23, Q24, Q25, Q26, Q27, Q28, Q29, Q30, Q31, Q32, Q33, Q34, Q35, Q36]), "depth" : 88 * mm, "offsetDistance" : 25 * mm});
        }
    });
